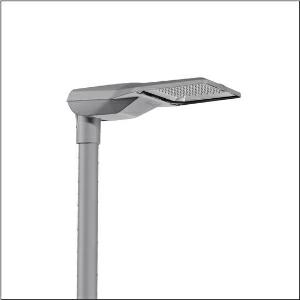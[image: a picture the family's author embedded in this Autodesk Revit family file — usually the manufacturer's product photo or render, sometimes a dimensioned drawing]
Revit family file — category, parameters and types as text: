
# Revit family: streetlight_sl_21_iq_midi___stw1_0a_5xe3e21g08nb_ca38
name_source: partatom
category: Lighting Fixtures
units: mm (PartAtom-declared; Revit-internal decimal feet)

## family parameters
Cut with Voids When Loaded = No
Host = Face
Light Source = No
Part Type = Normal
Room Calculation Point = No
Round Connector Dimension = Use Diameter
Shared = No

## types (1)
- --- (1 x LED, 19210 lm, 155.5 W, 2200K)
    Apparent Load = 155 VA
    CIE Flux Codes = 39 75 98 100 100
    Color Rendering = 70
    Color Temperature = 2200K
    Default Elevation = 1800 mm
    Description = Streetlight SL 21 iQ midi, mast luminaire, primary light control with lens, of PMMA, primary optical cover: cover, of toughened safety glass, transparent, light distribution: STW1.0a, light emission: direct distribution, primary light characteristic: asymmetric, installation type: post-top, side-entry, LED, High Power LED, rated luminous flux: 19.210lm, luminous efficacy: 124lm/W, light colour: 722, colour temperature: 2200K, control: Street-Remote, Auto-Match, Temp-Guard, Lumen-Switch, Night-Set, Smart-Wire, Light-Fading, Desk-Remote (wireless, voltage-free reading and setting of iQ features in the workshop via application-optimized NFC function/RFID function), optimised constant luminous flux control (CLO 2.0), presetting dimming linear, mains connection: 230..240V, AC, 50/60Hz, start of lifetime: 156W, end of service life: 162W, reduction: 69W, luminaire housing, of diecast aluminium, powder-coated, Siteco® metallic grey (DB 702S), corrosivity category C5 mid according to DIN EN ISO 12944, please order mast flange separately, inclination adjustable: 0°, 5°, 10°, 15°, sealing non-destructively replaceable, multi-level sealing system, length: 644mm, width: 335mm, height: 110mm, mast flange for spigot size: 42mm (side-entry): 5XC10008XM4, 60/48mm (side-entry/post-top): 5XC10108XM2, 76/60mm (side-entry/post-top): 5XC10108XM1, protection rating (complete): IP66, insulation class (complete): insulation class II (safety insulation), certification: CE, ENEC, ENEC+, VDE, impact resistance: IK09, permissible operating ambient temperature for outdoor applications: -40..+50°C, standard-compliant lighting for roads and squares, packaging unit: 1 piece

Light Distribution: STW1.0a
    Height = 111 mm
    Lamp = 1 x LED
    Lamp Light Flux = 19210 lm
    Lamp Power = 155.5 W
    Lamp count = 1
    Length = 644 mm
    Luminous efficacy = 124 lm/W
    Manufacturer = Siteco
    ModVariant = No
    Model = 5XE3E21G08NB
    Number of Poles = 1
    OnlyDefault = Yes
    Power Factor = 1
    Product Name = Streetlight SL 21 iQ midi | STW1.0a
    Product group = mast luminaire | pylon top
    ProductGroupID = 6100
    Protection Class = Protection class II
    Protection Degree = IP 66
    RLX_Detail_Level = 1
    RLX_Emergency_Light_Flux = 0 lm
    RLX_Emergency_Type = 0
    RLX_Emergency_Type_DB = No
    RlxData = <blob elided: 91213 chars, md5=f1363349>
    Socket = socket
    Standby Power = 0 W
    System Light Flux = 19210 lm
    System Power = 155 W
    Type Comments = factory setting: luminous flux: 100 % | dim-lin: 254 | 823 mA
    Type Image = l_1004298.jpg
    URL = http://relux.com
    VarID = @adj_120397
    Voltage = 0 V
    Weight = 0.00 kg
    Width = 336 mm

## geometry (parser evidence)
native form markers: Blend x4, Sweep x12
no freeform markers — native parametric forms only
